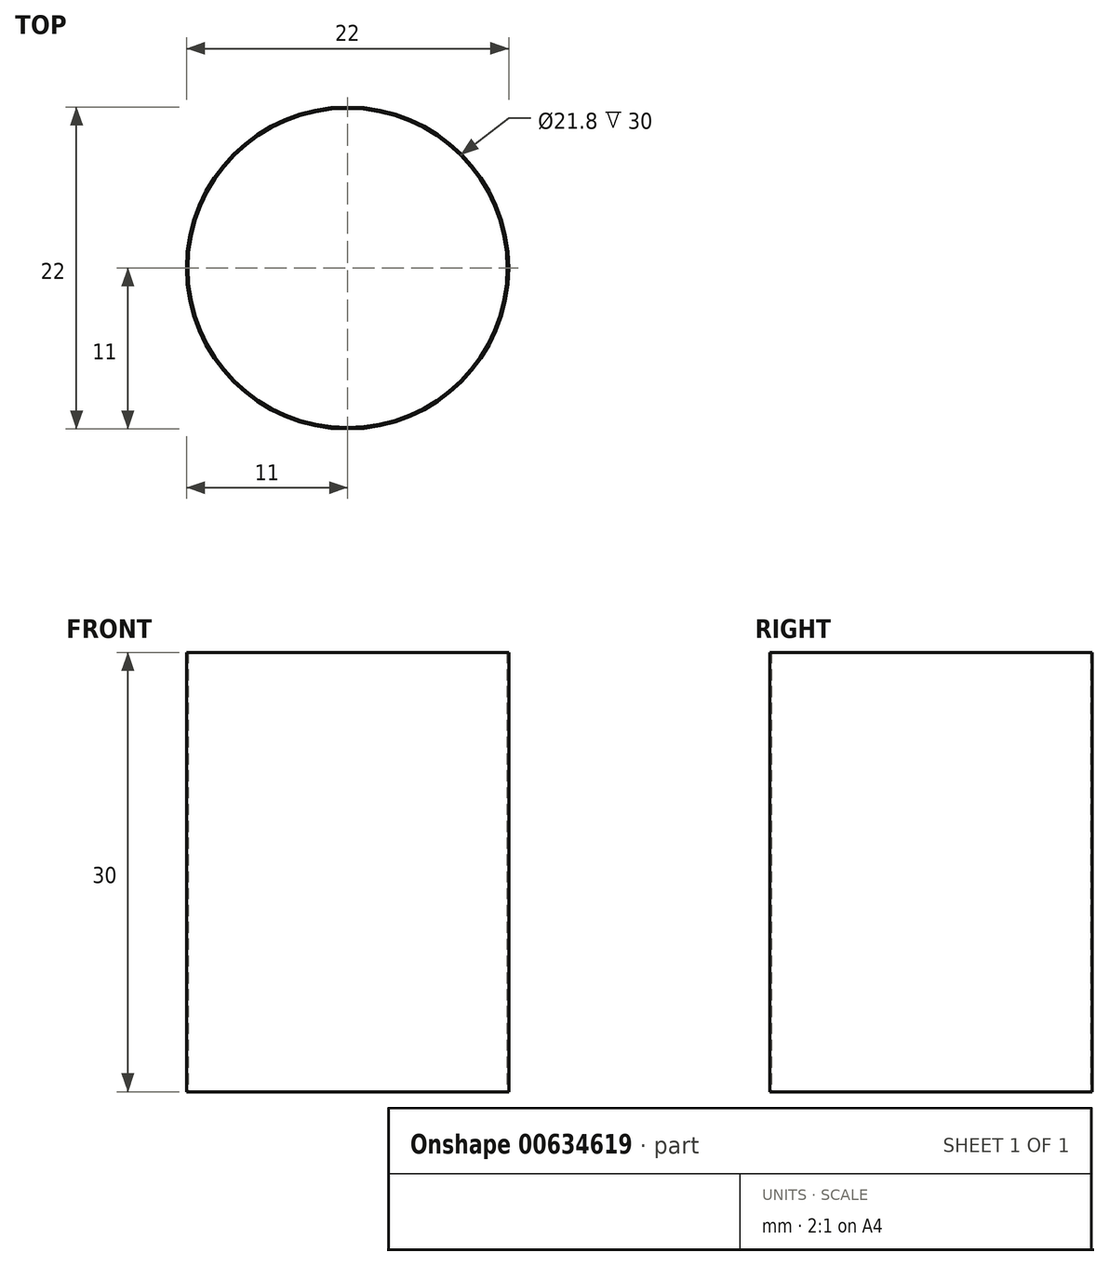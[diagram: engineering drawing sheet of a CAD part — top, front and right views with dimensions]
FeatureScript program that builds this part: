
annotation { "Feature Type Name" : "Feature", "Feature Type Description" : "" }
export const myFeature = defineFeature(function(context is Context, id is Id, definition is map)
    precondition{}
    {
        {
            var Q0;
            Q0=qCreatedBy(makeId("Top.planeOp"),FACE);
            var sketch = newSketch(context, id + "F0", { "sketchPlane" : qUnion([Q0])});
            skCircle(sketch, "E0", {"center": v(0, 0) * mm, "radius": 11 * mm});
            skCircle(sketch, "E1", {"center": v(0, 0) * mm, "radius": 10.9 * mm});
            skSolve(sketch);
        }
        {
            var Q0;
            Q0 = qSketchRegion(id + "F0", true);
            extrude(context, id + "F1", {"entities" : qUnion([Q0]), "depth" : 30 * mm, "offsetDistance" : 25 * mm});
        }
    });
